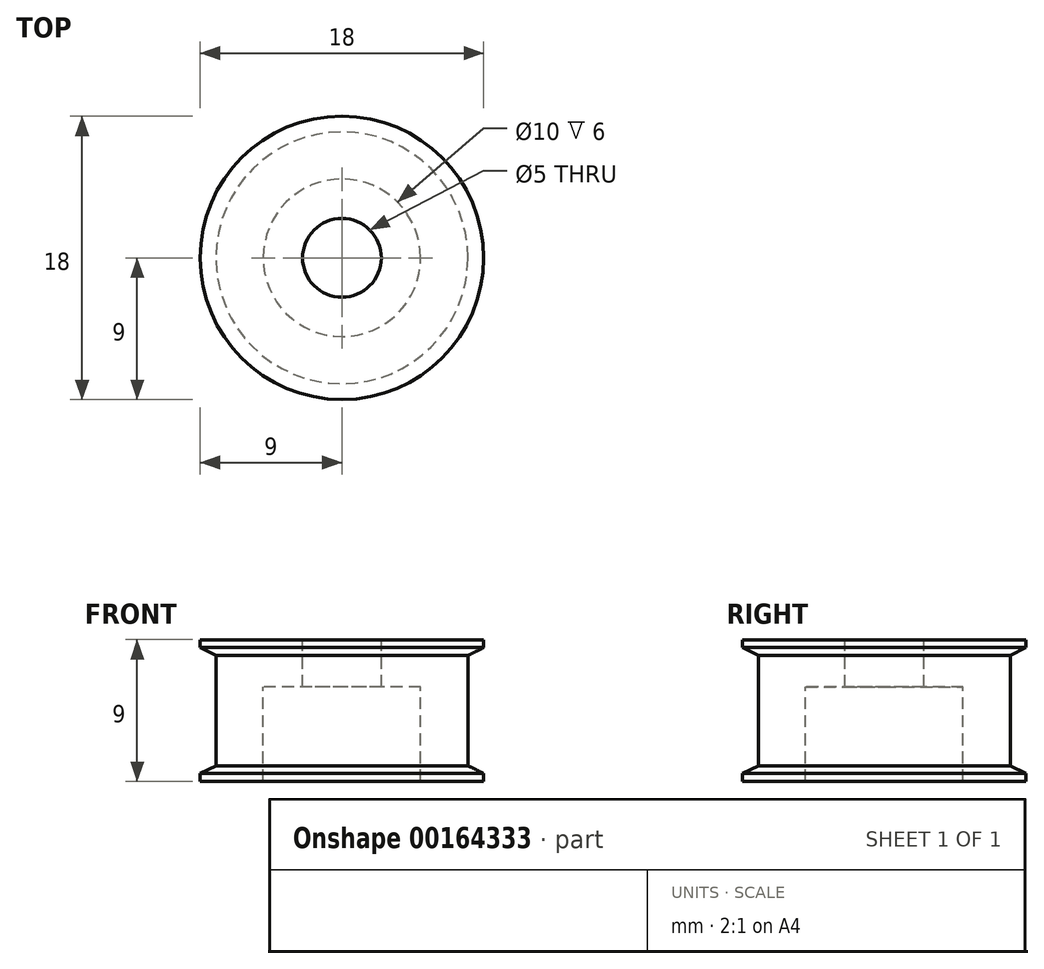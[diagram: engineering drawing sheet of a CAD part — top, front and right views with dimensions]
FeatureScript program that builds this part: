
annotation { "Feature Type Name" : "Feature", "Feature Type Description" : "" }
export const myFeature = defineFeature(function(context is Context, id is Id, definition is map)
    precondition{}
    {
        {
            var Q0;
            Q0=qCreatedBy(makeId("Front.planeOp"),FACE);
            var sketch = newSketch(context, id + "F0", { "sketchPlane" : qUnion([Q0])});
            skLineSegment(sketch, "E0", {"start": v(5, -7.51) * mm, "end": v(5, -1.51) * mm});
            skLineSegment(sketch, "E1", {"start": v(5, -1.51) * mm, "end": v(2.5, -1.51) * mm});
            skLineSegment(sketch, "E2", {"start": v(2.5, -1.51) * mm, "end": v(2.5, 1.49) * mm});
            skLineSegment(sketch, "E3", {"start": v(2.5, 1.49) * mm, "end": v(9, 1.49) * mm});
            skLineSegment(sketch, "E4", {"start": v(9, 1.49) * mm, "end": v(9, 0.99) * mm});
            skLineSegment(sketch, "E5", {"start": v(8, 0.49) * mm, "end": v(9, 0.99) * mm});
            skLineSegment(sketch, "E6", {"start": v(8, 0.49) * mm, "end": v(8, -6.51) * mm});
            skLineSegment(sketch, "E7", {"start": v(8, -6.51) * mm, "end": v(9, -7.01) * mm});
            skLineSegment(sketch, "E8", {"start": v(9, -7.01) * mm, "end": v(9, -7.51) * mm});
            skLineSegment(sketch, "E9", {"start": v(9, -7.51) * mm, "end": v(5, -7.51) * mm});
            skLineSegment(sketch, "E10", {"start": v(0, 0) * mm, "end": v(0, -3.64) * mm, "construction": true});
            skSolve(sketch);
        }
        {
            var Q0;
            Q0=makeQuery(id+"F0.imprint","IMPRINT",FACE,{"disambiguationData":[TD([[makeQuery(id+"F0.imprint","IMPRINT",EDGE,{"derivedFrom":sQuery(id+"F0.wireOp",EDGE,"E0")}),-1.0]])]});
            var Q1;
            Q1=sQuery(id+"F0.wireOp",EDGE,"E10");
            revolve(context, id + "F1", {"entities" : qUnion([Q0]), "axis" : qUnion([Q1]), "revolveType" : RevolveType.FULL});
        }
    });
